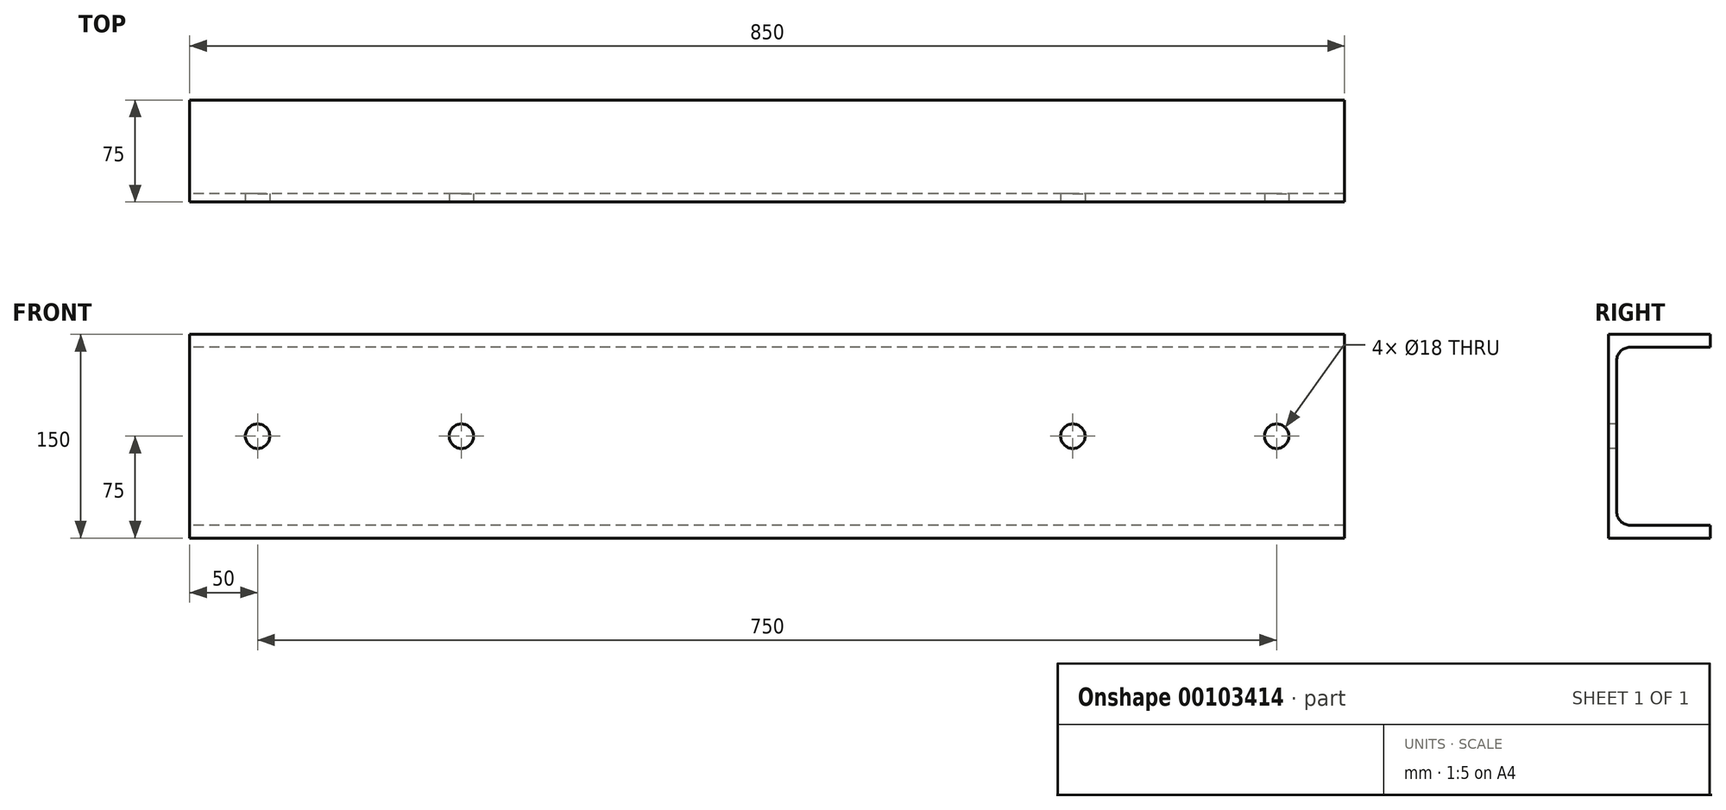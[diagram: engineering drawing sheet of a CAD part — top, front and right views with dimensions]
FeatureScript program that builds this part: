
annotation { "Feature Type Name" : "Feature", "Feature Type Description" : "" }
export const myFeature = defineFeature(function(context is Context, id is Id, definition is map)
    precondition{}
    {
        {
            var Q0;
            Q0=qCreatedBy(makeId("Right.planeOp"),FACE);
            var sketch = newSketch(context, id + "F0", { "sketchPlane" : qUnion([Q0])});
            skLineSegment(sketch, "E0", {"start": v(75, 0) * mm, "end": v(0, 0) * mm});
            skLineSegment(sketch, "E1", {"start": v(0, 0) * mm, "end": v(0, -150) * mm});
            skLineSegment(sketch, "E2", {"start": v(0, -150) * mm, "end": v(75, -150) * mm});
            skLineSegment(sketch, "E3", {"start": v(75, -150) * mm, "end": v(75, -140.5) * mm});
            skLineSegment(sketch, "E4", {"start": v(75, -140.5) * mm, "end": v(16, -140.5) * mm});
            skLineSegment(sketch, "E5", {"start": v(75, 0) * mm, "end": v(75, -9.5) * mm});
            skLineSegment(sketch, "E6", {"start": v(75, -9.5) * mm, "end": v(16, -9.5) * mm});
            skLineSegment(sketch, "E7", {"start": v(6, -19.5) * mm, "end": v(6, -130.5) * mm});
            skPoint(sketch, "E8.visualSharp", {"position": v(6, -9.5) * mm});
            skArc(sketch, "E8.filletArc", {"start": v(16, -9.5) * mm, "mid": v(8.93, -12.43) * mm, "end": v(6, -19.5) * mm});
            skPoint(sketch, "E9.visualSharp", {"position": v(6, -140.5) * mm});
            skArc(sketch, "E9.filletArc", {"start": v(6, -130.5) * mm, "mid": v(8.93, -137.57) * mm, "end": v(16, -140.5) * mm});
            skSolve(sketch);
        }
        {
            var Q0;
            Q0 = qSketchRegion(id + "F0", true);
            extrude(context, id + "F1", {"entities" : qUnion([Q0]), "endBound" : BoundingType.SYMMETRIC, "depth" : 850 * mm, "offsetDistance" : 25 * mm});
        }
        {
            var Q0;
            Q0=makeQuery(id+"F1.opExtrude","SWEPT_FACE",FACE,{"disambiguationData":[OSD([sQuery(id+"F0.wireOp",EDGE,"E1")])]});
            var sketch = newSketch(context, id + "F2", { "sketchPlane" : qUnion([Q0])});
            skCircle(sketch, "E10", {"center": v(-375, -75) * mm, "radius": 9 * mm});
            skCircle(sketch, "E11", {"center": v(-225, -75) * mm, "radius": 9 * mm});
            skCircle(sketch, "E12", {"center": v(225, -75) * mm, "radius": 9 * mm});
            skCircle(sketch, "E13", {"center": v(375, -75) * mm, "radius": 9 * mm});
            skSolve(sketch);
        }
        {
            var Q0;
            Q0 = qSketchRegion(id + "F2", true);
            extrude(context, id + "F3", {"entities" : qUnion([Q0]), "operationType" : NewBodyOperationType.REMOVE, "oppositeDirection" : true, "depth" : 25 * mm, "offsetDistance" : 25 * mm});
        }
    });
